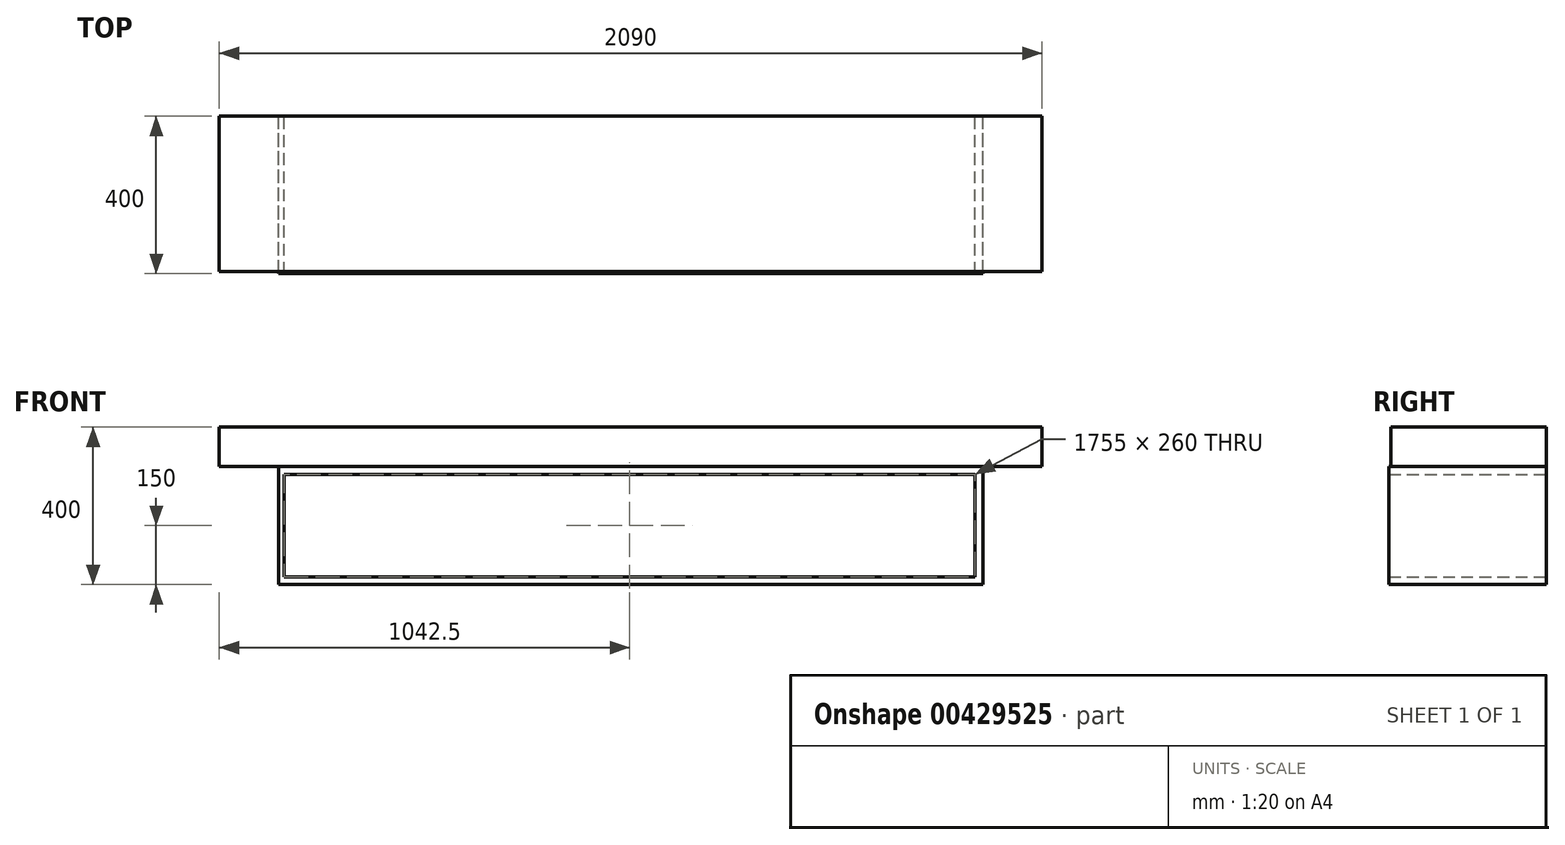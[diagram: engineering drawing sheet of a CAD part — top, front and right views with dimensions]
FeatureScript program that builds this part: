
annotation { "Feature Type Name" : "Feature", "Feature Type Description" : "" }
export const myFeature = defineFeature(function(context is Context, id is Id, definition is map)
    precondition{}
    {
        {
            var Q0;
            Q0=qCreatedBy(makeId("Front.planeOp"),FACE);
            var sketch = newSketch(context, id + "F0", { "sketchPlane" : qUnion([Q0])});
            skLineSegment(sketch, "E0.bottom", {"start": v(1045, -50) * mm, "end": v(-1045, -50) * mm});
            skLineSegment(sketch, "E0.top", {"start": v(1045, 50) * mm, "end": v(-1045, 50) * mm});
            skLineSegment(sketch, "E0.left", {"start": v(1045, -50) * mm, "end": v(1045, 50) * mm});
            skLineSegment(sketch, "E0.right", {"start": v(-1045, -50) * mm, "end": v(-1045, 50) * mm});
            skPoint(sketch, "E0.middle", {"position": v(0, 0) * mm});
            skLineSegment(sketch, "E1.0", {"start": v(895, -350) * mm, "end": v(-145, -350) * mm});
            skLineSegment(sketch, "E2.0", {"start": v(-405, -50) * mm, "end": v(-405, 50) * mm, "construction": true});
            skLineSegment(sketch, "E3", {"start": v(-405, -50) * mm, "end": v(-405, -638.82) * mm, "construction": true});
            skLineSegment(sketch, "E4.0", {"start": v(420, -50) * mm, "end": v(420, 50) * mm, "construction": true});
            skLineSegment(sketch, "E5", {"start": v(420, -50) * mm, "end": v(420, -646.01) * mm, "construction": true});
            skLineSegment(sketch, "E6", {"start": v(-895, -50) * mm, "end": v(-895, -350) * mm});
            skLineSegment(sketch, "E7", {"start": v(895, -50) * mm, "end": v(895, -350) * mm});
            skLineSegment(sketch, "E8.trimOffspring", {"start": v(-145, -350) * mm, "end": v(-895, -350) * mm});
            skLineSegment(sketch, "E9.0", {"start": v(-145, -330) * mm, "end": v(-895, -330) * mm});
            skLineSegment(sketch, "E10.0", {"start": v(-5, -50) * mm, "end": v(-5, -350) * mm});
            skLineSegment(sketch, "E11.0", {"start": v(895, -330) * mm, "end": v(-145, -330) * mm});
            skLineSegment(sketch, "E12.0", {"start": v(875, -50) * mm, "end": v(875, -350) * mm});
            skLineSegment(sketch, "E13.0", {"start": v(895, -70) * mm, "end": v(145, -70) * mm});
            skLineSegment(sketch, "E14.trimOffspring", {"start": v(-145, -70) * mm, "end": v(-895, -70) * mm});
            skLineSegment(sketch, "E15", {"start": v(145, -70) * mm, "end": v(-145, -70) * mm});
            skLineSegment(sketch, "E16.0", {"start": v(-880, -50) * mm, "end": v(-880, -350) * mm});
            skSolve(sketch);
        }
        {
            var Q0;
            {var subQ0=sQuery(id+"F0.wireOp",EDGE,"E9.0");var subQ1=sQuery(id+"F0.wireOp",EDGE,"TmIEvhIl-2B60-tP35-RM89-IO3GquMOMQva");var subQ2=makeQuery(id+"F0.imprint","INTERSECT",VERTEX,{"derivedFrom":[subQ1,subQ0]});Q0=makeQuery(id+"F0.imprint","IMPRINT",FACE,{"disambiguationData":[TD([[makeQuery(id+"F0.imprint","IMPRINT",EDGE,{"disambiguationData":[TD([[subQ2,1.0]])],"derivedFrom":subQ1}),-1.0]])]});}
            var Q1;
            {var subQ0=sQuery(id+"F0.wireOp",EDGE,"TmIEvhIl-2B60-tP35-RM89-IO3GquMOMQva");var subQ1=sQuery(id+"F0.wireOp",EDGE,"E0.bottom");var subQ2=makeQuery(id+"F0.imprint","INTERSECT",VERTEX,{"derivedFrom":[subQ1,subQ0]});Q1=makeQuery(id+"F0.imprint","IMPRINT",FACE,{"disambiguationData":[TD([[makeQuery(id+"F0.imprint","IMPRINT",EDGE,{"disambiguationData":[TD([[subQ2,-1.0]])],"derivedFrom":subQ1}),1.0]])]});}
            var Q2;
            {var subQ0=sQuery(id+"F0.wireOp",EDGE,"E8.trimOffspring");var subQ1=sQuery(id+"F0.wireOp",EDGE,"TmIEvhIl-2B60-tP35-RM89-IO3GquMOMQva");var subQ2=makeQuery(id+"F0.imprint","INTERSECT",VERTEX,{"derivedFrom":[subQ1,subQ0]});Q2=makeQuery(id+"F0.imprint","IMPRINT",FACE,{"disambiguationData":[TD([[makeQuery(id+"F0.imprint","IMPRINT",EDGE,{"disambiguationData":[TD([[subQ2,1.0]])],"derivedFrom":subQ1}),-1.0]])]});}
            var Q3;
            {var subQ0=sQuery(id+"F0.wireOp",EDGE,"62d9af77-1868-4837-a746-32d6302984bc.0");var subQ1=sQuery(id+"F0.wireOp",EDGE,"E8.trimOffspring");var subQ2=makeQuery(id+"F0.imprint","INTERSECT",VERTEX,{"derivedFrom":[subQ1,subQ0]});Q3=makeQuery(id+"F0.imprint","IMPRINT",FACE,{"disambiguationData":[TD([[makeQuery(id+"F0.imprint","IMPRINT",EDGE,{"disambiguationData":[TD([[subQ2,-1.0]])],"derivedFrom":subQ1}),-1.0]])]});}
            var Q4;
            {var subQ0=sQuery(id+"F0.wireOp",EDGE,"E8.trimOffspring");var subQ1=sQuery(id+"F0.wireOp",EDGE,"E6");var subQ2=makeQuery(id+"F0.imprint","INTERSECT",VERTEX,{"derivedFrom":[subQ1,subQ0]});Q4=makeQuery(id+"F0.imprint","IMPRINT",FACE,{"disambiguationData":[TD([[makeQuery(id+"F0.imprint","IMPRINT",EDGE,{"disambiguationData":[TD([[subQ2,1.0]])],"derivedFrom":subQ1}),1.0]])]});}
            var Q5;
            {var subQ0=sQuery(id+"F0.wireOp",EDGE,"E9.0");var subQ1=sQuery(id+"F0.wireOp",EDGE,"E6");var subQ2=makeQuery(id+"F0.imprint","INTERSECT",VERTEX,{"derivedFrom":[subQ1,subQ0]});Q5=makeQuery(id+"F0.imprint","IMPRINT",FACE,{"disambiguationData":[TD([[makeQuery(id+"F0.imprint","IMPRINT",EDGE,{"disambiguationData":[TD([[subQ2,1.0]])],"derivedFrom":subQ1}),1.0]])]});}
            var Q6;
            {var subQ0=sQuery(id+"F0.wireOp",EDGE,"E6");var subQ1=sQuery(id+"F0.wireOp",EDGE,"E0.bottom");var subQ2=makeQuery(id+"F0.imprint","INTERSECT",VERTEX,{"derivedFrom":[subQ1,subQ0]});Q6=makeQuery(id+"F0.imprint","IMPRINT",FACE,{"disambiguationData":[TD([[makeQuery(id+"F0.imprint","IMPRINT",EDGE,{"disambiguationData":[TD([[subQ2,1.0]])],"derivedFrom":subQ1}),1.0]])]});}
            var Q7;
            {var subQ0=sQuery(id+"F0.wireOp",EDGE,"62d9af77-1868-4837-a746-32d6302984bc.0");var subQ1=sQuery(id+"F0.wireOp",EDGE,"E0.bottom");var subQ2=makeQuery(id+"F0.imprint","INTERSECT",VERTEX,{"derivedFrom":[subQ1,subQ0]});Q7=makeQuery(id+"F0.imprint","IMPRINT",FACE,{"disambiguationData":[TD([[makeQuery(id+"F0.imprint","IMPRINT",EDGE,{"disambiguationData":[TD([[subQ2,-1.0]])],"derivedFrom":subQ1}),1.0]])]});}
            var Q8;
            {var subQ0=sQuery(id+"F0.wireOp",EDGE,"E11.0");var subQ1=sQuery(id+"F0.wireOp",EDGE,"veNjtBWM-l1l4-6HnX-swN3-JSQbFiMoUbJ6");var subQ2=makeQuery(id+"F0.imprint","INTERSECT",VERTEX,{"derivedFrom":[subQ1,subQ0]});Q8=makeQuery(id+"F0.imprint","IMPRINT",FACE,{"disambiguationData":[TD([[makeQuery(id+"F0.imprint","IMPRINT",EDGE,{"disambiguationData":[TD([[subQ2,1.0]])],"derivedFrom":subQ1}),1.0]])]});}
            var Q9;
            {var subQ0=sQuery(id+"F0.wireOp",EDGE,"veNjtBWM-l1l4-6HnX-swN3-JSQbFiMoUbJ6");var subQ1=sQuery(id+"F0.wireOp",EDGE,"E0.bottom");var subQ2=makeQuery(id+"F0.imprint","INTERSECT",VERTEX,{"derivedFrom":[subQ1,subQ0]});Q9=makeQuery(id+"F0.imprint","IMPRINT",FACE,{"disambiguationData":[TD([[makeQuery(id+"F0.imprint","IMPRINT",EDGE,{"disambiguationData":[TD([[subQ2,1.0]])],"derivedFrom":subQ1}),1.0]])]});}
            var Q10;
            {var subQ0=sQuery(id+"F0.wireOp",EDGE,"veNjtBWM-l1l4-6HnX-swN3-JSQbFiMoUbJ6");var subQ1=sQuery(id+"F0.wireOp",EDGE,"E1.0");var subQ2=makeQuery(id+"F0.imprint","INTERSECT",VERTEX,{"derivedFrom":[subQ1,subQ0]});Q10=makeQuery(id+"F0.imprint","IMPRINT",FACE,{"disambiguationData":[TD([[makeQuery(id+"F0.imprint","IMPRINT",EDGE,{"disambiguationData":[TD([[subQ2,1.0]])],"derivedFrom":subQ1}),-1.0]])]});}
            var Q11;
            {var subQ0=sQuery(id+"F0.wireOp",EDGE,"2e549250-9ff1-4f53-9318-fb78c61b1356.0");var subQ1=sQuery(id+"F0.wireOp",EDGE,"E1.0");var subQ2=makeQuery(id+"F0.imprint","INTERSECT",VERTEX,{"derivedFrom":[subQ1,subQ0]});Q11=makeQuery(id+"F0.imprint","IMPRINT",FACE,{"disambiguationData":[TD([[makeQuery(id+"F0.imprint","IMPRINT",EDGE,{"disambiguationData":[TD([[subQ2,1.0]])],"derivedFrom":subQ1}),-1.0]])]});}
            var Q12;
            {var subQ0=sQuery(id+"F0.wireOp",EDGE,"2e549250-9ff1-4f53-9318-fb78c61b1356.0");var subQ1=sQuery(id+"F0.wireOp",EDGE,"E0.bottom");var subQ2=makeQuery(id+"F0.imprint","INTERSECT",VERTEX,{"derivedFrom":[subQ1,subQ0]});Q12=makeQuery(id+"F0.imprint","IMPRINT",FACE,{"disambiguationData":[TD([[makeQuery(id+"F0.imprint","IMPRINT",EDGE,{"disambiguationData":[TD([[subQ2,1.0]])],"derivedFrom":subQ1}),1.0]])]});}
            var Q13;
            {var subQ0=sQuery(id+"F0.wireOp",EDGE,"E7");var subQ1=sQuery(id+"F0.wireOp",EDGE,"E0.bottom");var subQ2=makeQuery(id+"F0.imprint","INTERSECT",VERTEX,{"derivedFrom":[subQ1,subQ0]});Q13=makeQuery(id+"F0.imprint","IMPRINT",FACE,{"disambiguationData":[TD([[makeQuery(id+"F0.imprint","IMPRINT",EDGE,{"disambiguationData":[TD([[subQ2,-1.0]])],"derivedFrom":subQ1}),1.0]])]});}
            var Q14;
            {var subQ0=sQuery(id+"F0.wireOp",EDGE,"E11.0");var subQ1=sQuery(id+"F0.wireOp",EDGE,"E7");var subQ2=makeQuery(id+"F0.imprint","INTERSECT",VERTEX,{"derivedFrom":[subQ1,subQ0]});Q14=makeQuery(id+"F0.imprint","IMPRINT",FACE,{"disambiguationData":[TD([[makeQuery(id+"F0.imprint","IMPRINT",EDGE,{"disambiguationData":[TD([[subQ2,1.0]])],"derivedFrom":subQ1}),-1.0]])]});}
            var Q15;
            {var subQ0=sQuery(id+"F0.wireOp",EDGE,"E7");var subQ1=sQuery(id+"F0.wireOp",EDGE,"E1.0");var subQ2=makeQuery(id+"F0.imprint","INTERSECT",VERTEX,{"derivedFrom":[subQ1,subQ0]});Q15=makeQuery(id+"F0.imprint","IMPRINT",FACE,{"disambiguationData":[TD([[makeQuery(id+"F0.imprint","IMPRINT",EDGE,{"disambiguationData":[TD([[subQ2,-1.0]])],"derivedFrom":subQ1}),-1.0]])]});}
            var Q16;
            {var subQ1=sQuery(id+"F0.wireOp",EDGE,"E8.trimOffspring");var subQ7=sQuery(id+"F0.wireOp",EDGE,"E1.0");var subQ8=makeQuery(id+"F0.imprint","INTERSECT",VERTEX,{"derivedFrom":[subQ7,subQ1]});Q16=makeQuery(id+"F0.imprint","IMPRINT",FACE,{"disambiguationData":[TD([[makeQuery(id+"F0.imprint","IMPRINT",EDGE,{"disambiguationData":[TD([[subQ8,1.0]])],"derivedFrom":subQ7}),-1.0]])]});}
            var Q17;
            {var subQ0=sQuery(id+"F0.wireOp",EDGE,"E15");Q17=makeQuery(id+"F0.imprint","IMPRINT",FACE,{"disambiguationData":[TD([[makeQuery(id+"F0.imprint","IMPRINT",EDGE,{"derivedFrom":subQ0}),-1.0]])]});}
            extrude(context, id + "F1", {"entities" : qUnion([Q0, Q1, Q2, Q3, Q4, Q5, Q6, Q7, Q8, Q9, Q10, Q11, Q12, Q13, Q14, Q15, Q16, Q17]), "depth" : 400 * mm});
        }
        {
            var Q0;
            Q0=makeQuery(id+"F0.imprint","IMPRINT",FACE,{"disambiguationData":[TD([[makeQuery(id+"F0.imprint","IMPRINT",EDGE,{"derivedFrom":sQuery(id+"F0.wireOp",EDGE,"E0.top")}),1.0]])]});
            extrude(context, id + "F2", {"entities" : qUnion([Q0]), "operationType" : NewBodyOperationType.ADD, "depth" : 395 * mm});
        }
    });
